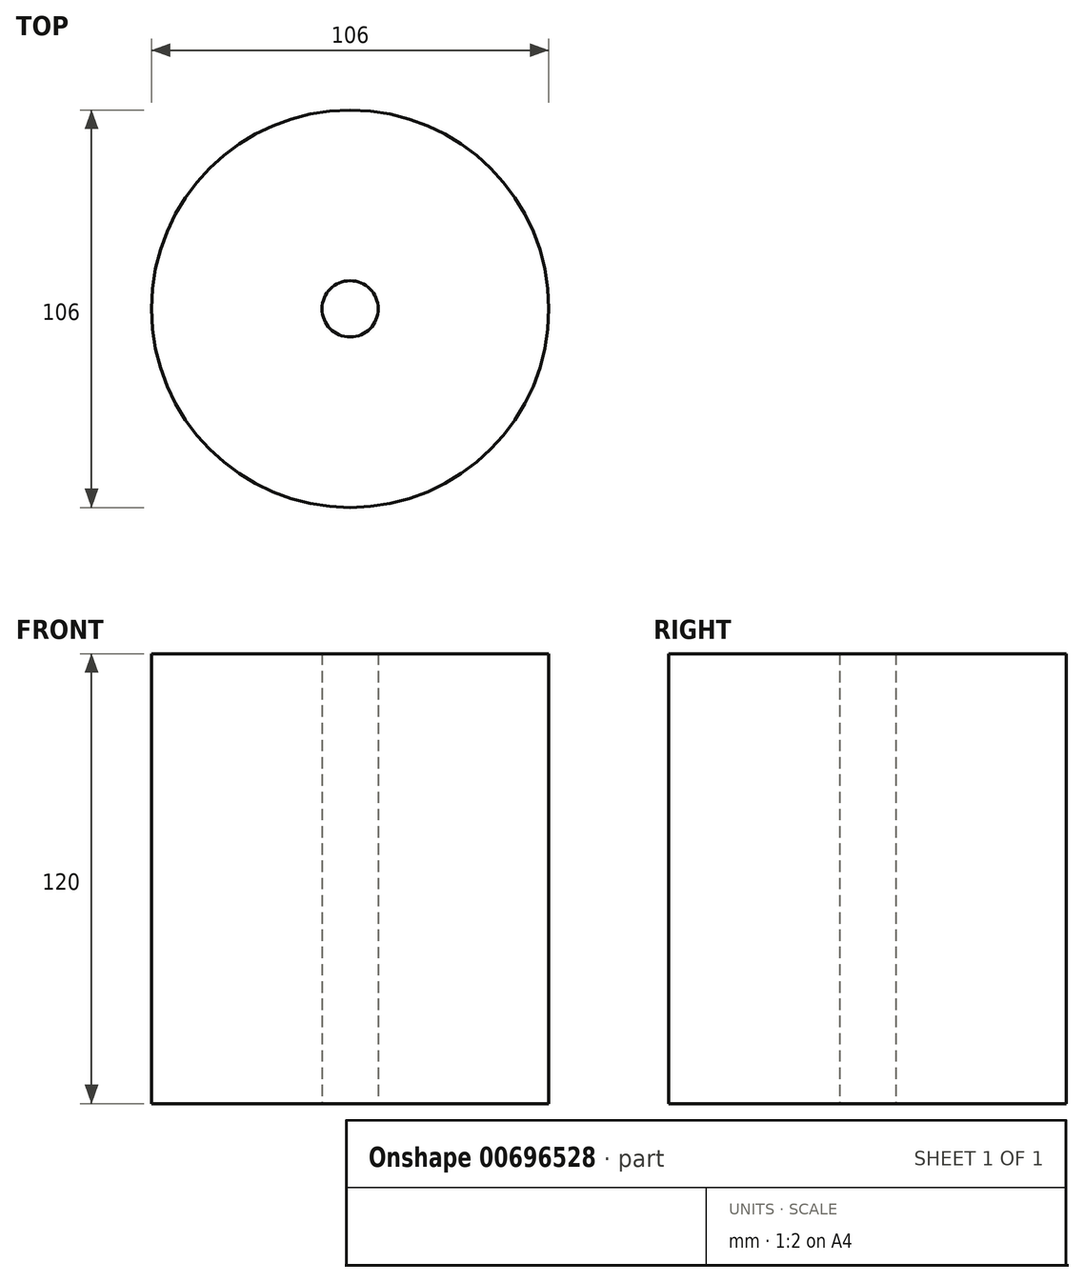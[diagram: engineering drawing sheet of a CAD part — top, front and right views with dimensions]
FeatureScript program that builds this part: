
annotation { "Feature Type Name" : "Feature", "Feature Type Description" : "" }
export const myFeature = defineFeature(function(context is Context, id is Id, definition is map)
    precondition{}
    {
        {
            var Q0;
            Q0=qCreatedBy(makeId("Top.planeOp"),FACE);
            var sketch = newSketch(context, id + "F0", { "sketchPlane" : qUnion([Q0])});
            skCircle(sketch, "E0", {"center": v(0, 0) * mm, "radius": 59.5 * mm});
            skCircle(sketch, "E1", {"center": v(0, 0) * mm, "radius": 53 * mm});
            skCircle(sketch, "E2", {"center": v(0, 0) * mm, "radius": 7.5 * mm});
            skSolve(sketch);
        }
        {
            var Q0;
            Q0=sQuery(id+"F0.wireOp",EDGE,"E0");
            extrude(context, id + "F1", {"bodyType" : ToolBodyType.SURFACE, "surfaceEntities" : qUnion([Q0]), "depth" : 120 * mm, "offsetDistance" : 25 * mm});
        }
        {
            var Q0;
            Q0=makeQuery(id+"F0.imprint","IMPRINT",FACE,{"disambiguationData":[TD([[makeQuery(id+"F0.imprint","IMPRINT",EDGE,{"derivedFrom":sQuery(id+"F0.wireOp",EDGE,"E1")}),1.0]])]});
            extrude(context, id + "F2", {"entities" : qUnion([Q0]), "depth" : 120 * mm, "offsetDistance" : 25 * mm});
        }
    });
